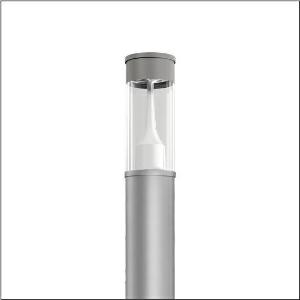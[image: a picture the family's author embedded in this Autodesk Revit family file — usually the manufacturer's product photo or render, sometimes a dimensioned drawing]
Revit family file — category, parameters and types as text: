
# Revit family: city-light_260_iq___pl1_2s_5xa5295rf14h_a018
name_source: partatom
category: Lighting Fixtures
units: mm (PartAtom-declared; Revit-internal decimal feet)

## family parameters
Cut with Voids When Loaded = No
Host = Face
Light Source = No
Part Type = Normal
Room Calculation Point = No
Round Connector Dimension = Use Diameter
Shared = No

## types (1)
- --- (1 x LED, 2970 lm, 18.5 W, 4000K)
    Apparent Load = 19 VA
    CIE Flux Codes = 23 62 94 96 100
    Color Rendering = 70
    Color Temperature = 4000K
    Default Elevation = 1800 mm
    Description = City-Light 260 iQ, light pillar, Module 540 iQ-SR, primary light control with 3 zone facetted reflector, of plastic, silver coated, highly specular, structured, primary optical cover: cover, of PMMA, transparent, partly coated, light distribution: PL1.2s, primary light characteristic: symmetric, LED, High Power LED, rated luminous flux: 2.970lm, luminous efficacy: 161lm/W, light colour: 740, colour temperature: 4000K, control gear: iQ Street-Remote, control: pre-setting: logarithmic dimming characteristic, Street-Remote, Auto-Match, Temp-Guard, Lumen-Switch, Night-Set, Smart-Wire, Light-Fading, Desk-Remote (wireless, voltage-free reading and setting of iQ features in the workshop via application-optimized NFC function/RFID function), optimised constant luminous flux control (CLO 2.0), with terminal, 6-pole, max. 2.5mm², mains connection: 230..240V, AC, 50/60Hz, start of lifetime: 19W, end of service life: 20W, reduction: 9W, luminaire housing, cylindrical, of extruded aluminium section, coated, Siteco® metallic grey (DB 702S), length: 2.600mm, diameter: 200mm, Module 540 iQ-SR, traffic white (RAL 9016), equipment: standard, protection rating (complete): IP65, insulation class (complete): insulation class II (safety insulation), certification: CE, ENEC, VDE, packaging unit: 1 piece

Light Distribution: PL1.2s
    Height = 500 mm
    Lamp = 1 x LED
    Lamp Light Flux = 2970 lm
    Lamp Power = 18.5 W
    Lamp count = 1
    Length = 200 mm  [stored 0.656168 ft]
    Luminous efficacy = 161 lm/W
    Manufacturer = Siteco
    ModVariant = No
    Model = 5XA5295RF14H
    Mounting Place = Floor
    Mounting Type = Freestanding
    Number of Poles = 1
    OnlyDefault = Yes
    Power Factor = 1
    Product Name = City-Light 260 iQ | PL1.2s
    Product group = light pillar
    ProductGroupID = 1301
    Protection Class = Protection class II
    Protection Degree = IP 65
    RLX_Detail_Level = 1
    RLX_Emergency_Light_Flux = 0 lm
    RLX_Emergency_Type = 0
    RLX_Emergency_Type_DB = No
    RlxData = <blob elided: 28785 chars, md5=9f549d6d>
    Socket = socket
    Standby Power = 0 W
    System Light Flux = 2970 lm
    System Power = 19 W
    Type Comments = factory setting: luminous flux: 100 % | dim-lin: 254 | 385 mA
    Type Image = l_1006920.jpg
    URL = http://relux.com
    VarID = @adj_146099
    Voltage = 0 V
    Weight = 0.00 kg
    Width = 0 mm  [stored 0 ft]

note: [stored X ft] marks values corroborated as IEEE doubles in the binary element streams (Revit-internal decimal feet)

## geometry (parser evidence)
native form markers: Blend x4, Sweep x8
no freeform markers — native parametric forms only
